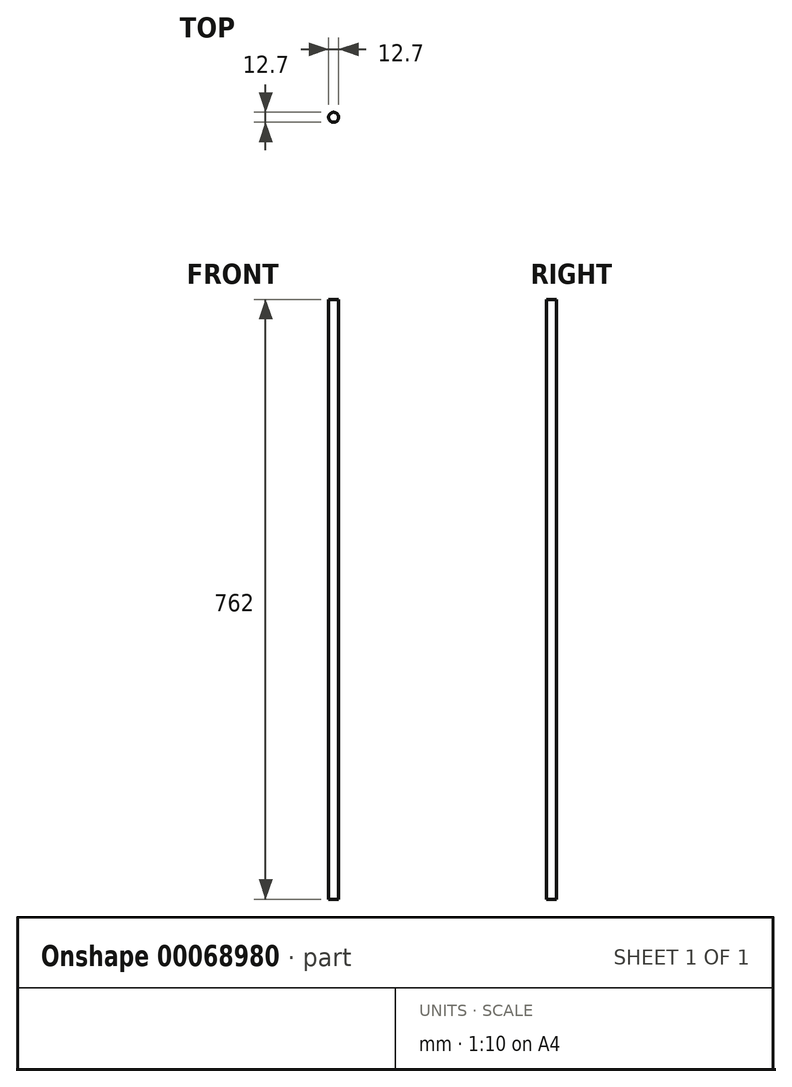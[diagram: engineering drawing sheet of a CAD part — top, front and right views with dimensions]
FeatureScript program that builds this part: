
annotation { "Feature Type Name" : "Feature", "Feature Type Description" : "" }
export const myFeature = defineFeature(function(context is Context, id is Id, definition is map)
    precondition{}
    {
        {
            var Q0;
            Q0=qCreatedBy(makeId("Front.planeOp"),FACE);
            var sketch = newSketch(context, id + "F0", { "sketchPlane" : qUnion([Q0])});
            skLineSegment(sketch, "E0.bottom", {"start": v(0, 0) * mm, "end": v(6.35, 0) * mm});
            skLineSegment(sketch, "E0.top", {"start": v(0, 762) * mm, "end": v(6.35, 762) * mm});
            skLineSegment(sketch, "E0.left", {"start": v(0, 0) * mm, "end": v(0, 762) * mm});
            skLineSegment(sketch, "E0.right", {"start": v(6.35, 0) * mm, "end": v(6.35, 762) * mm});
            skSolve(sketch);
        }
        {
            var Q0;
            Q0 = qSketchRegion(id + "F0", true);
            var Q1;
            Q1=sQuery(id+"F0.wireOp",EDGE,"E0.left");
            revolve(context, id + "F1", {"entities" : qUnion([Q0]), "axis" : qUnion([Q1]), "revolveType" : RevolveType.ONE_DIRECTION, "angle" : 360 * degree});
        }
    });
